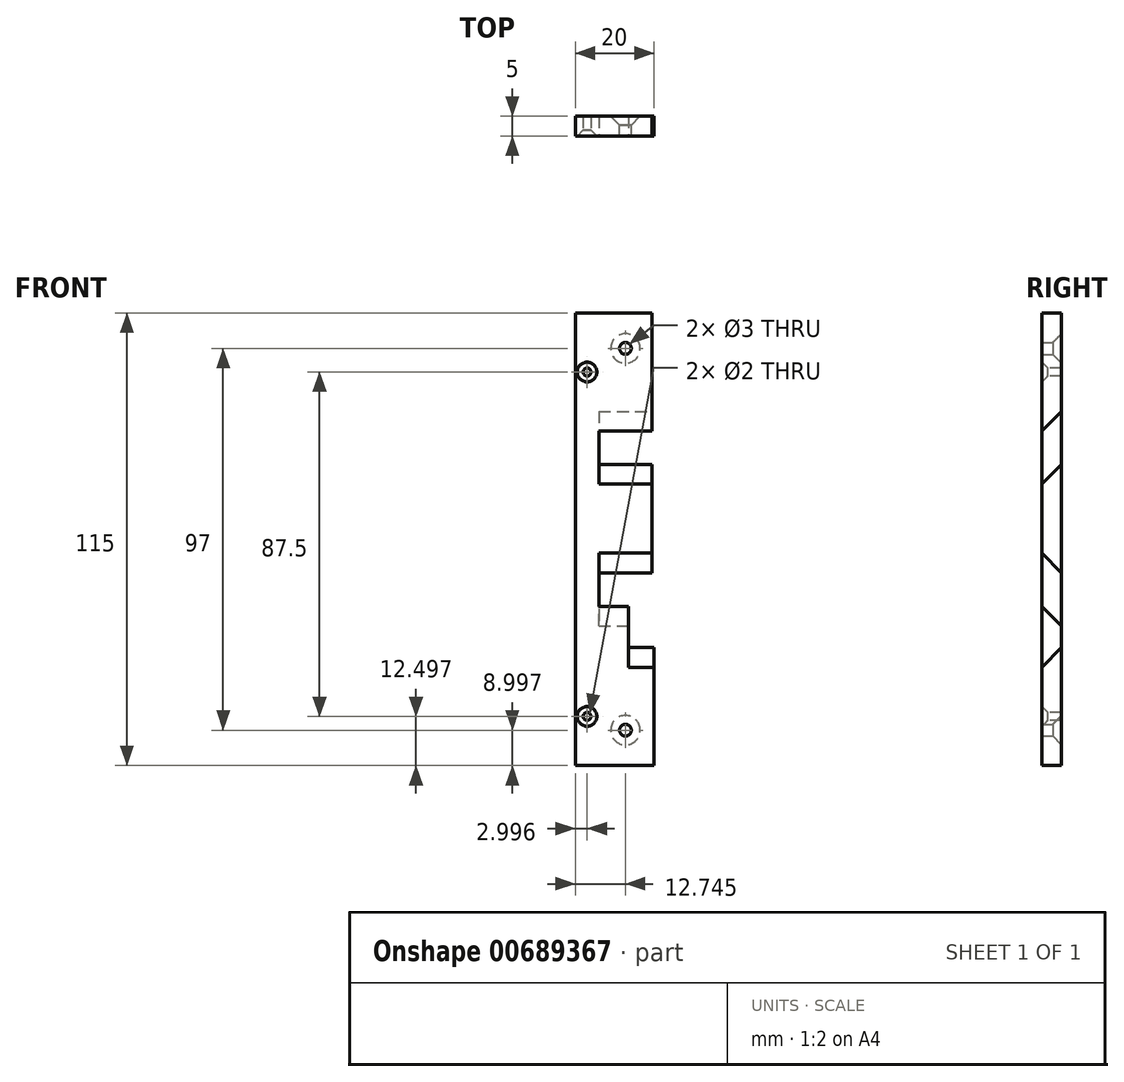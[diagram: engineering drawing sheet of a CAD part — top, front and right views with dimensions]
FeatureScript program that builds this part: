
annotation { "Feature Type Name" : "Feature", "Feature Type Description" : "" }
export const myFeature = defineFeature(function(context is Context, id is Id, definition is map)
    precondition{}
    {
        {
            var Q0;
            Q0=qCreatedBy(makeId("Front.planeOp"),FACE);
            var sketch = newSketch(context, id + "F0", { "sketchPlane" : qUnion([Q0])});
            skLineSegment(sketch, "E0.top", {"start": v(-0.37, 114.33) * mm, "end": v(19.13, 114.33) * mm});
            skLineSegment(sketch, "E0.left", {"start": v(-0.37, -0.67) * mm, "end": v(-0.37, 114.33) * mm});
            skLineSegment(sketch, "E1", {"start": v(5.63, 84.33) * mm, "end": v(5.63, 75.83) * mm});
            skLineSegment(sketch, "E2", {"start": v(5.63, 84.33) * mm, "end": v(19.13, 84.33) * mm});
            skLineSegment(sketch, "E3.trimOffspring", {"start": v(5.63, 48.33) * mm, "end": v(5.63, 39.83) * mm});
            skLineSegment(sketch, "E4", {"start": v(19.13, 114.33) * mm, "end": v(19.13, 84.33) * mm});
            skLineSegment(sketch, "E5.trimOffspring", {"start": v(19.13, 75.83) * mm, "end": v(5.63, 75.83) * mm});
            skLineSegment(sketch, "E6.trimOffspring", {"start": v(19.13, 48.33) * mm, "end": v(5.63, 48.33) * mm});
            skLineSegment(sketch, "E7.trimOffspring", {"start": v(19.63, 29.33) * mm, "end": v(13.13, 29.33) * mm});
            skLineSegment(sketch, "E8", {"start": v(19.63, 29.33) * mm, "end": v(19.63, -0.67) * mm});
            skLineSegment(sketch, "E9", {"start": v(13.13, 29.33) * mm, "end": v(13.13, 39.83) * mm});
            skLineSegment(sketch, "E10.trimOffspring", {"start": v(13.13, 39.83) * mm, "end": v(5.63, 39.83) * mm});
            skLineSegment(sketch, "E11.trimOffspring", {"start": v(19.13, 75.83) * mm, "end": v(19.13, 48.33) * mm});
            skLineSegment(sketch, "E12", {"start": v(-0.37, -0.67) * mm, "end": v(19.63, -0.67) * mm});
            skSolve(sketch);
        }
        {
            var Q0;
            Q0=qSketchRegion(id+"F0",true);
            extrude(context, id + "F1", {"entities" : qUnion([Q0]), "depth" : 5 * mm});
        }
        {
            var Q0;
            Q0=makeQuery(id+"F1.opExtrude","SWEPT_FACE",FACE,{"disambiguationData":[OSD([sQuery(id+"F0.wireOp",EDGE,"E4")])]});
            var sketch = newSketch(context, id + "F2", { "sketchPlane" : qUnion([Q0])});
            skLineSegment(sketch, "E13", {"start": v(-5, 84.33) * mm, "end": v(0, 84.33) * mm});
            skLineSegment(sketch, "E14", {"start": v(0, 84.33) * mm, "end": v(0, 89.33) * mm});
            skLineSegment(sketch, "E15", {"start": v(0, 89.33) * mm, "end": v(-5, 84.33) * mm});
            skSolve(sketch);
        }
        {
            var Q0;
            Q0=makeQuery(id+"F1.opExtrude","SWEPT_FACE",FACE,{"disambiguationData":[OSD([sQuery(id+"F0.wireOp",EDGE,"E11.trimOffspring")])]});
            var sketch = newSketch(context, id + "F3", { "sketchPlane" : qUnion([Q0])});
            skLineSegment(sketch, "E16", {"start": v(0, 75.83) * mm, "end": v(-5, 75.83) * mm});
            skLineSegment(sketch, "E17", {"start": v(-5, 75.83) * mm, "end": v(-5, 70.83) * mm});
            skLineSegment(sketch, "E18", {"start": v(-5, 70.83) * mm, "end": v(0, 75.83) * mm});
            skLineSegment(sketch, "E19", {"start": v(0, 48.33) * mm, "end": v(-5, 48.33) * mm});
            skLineSegment(sketch, "E20", {"start": v(-5, 48.33) * mm, "end": v(-5, 53.33) * mm});
            skLineSegment(sketch, "E21", {"start": v(-5, 53.33) * mm, "end": v(0, 48.33) * mm});
            skSolve(sketch);
        }
        {
            var Q0;
            Q0=qSketchRegion(id+"F2",true);
            var Q1;
            Q1=qSketchRegion(id+"F3",true);
            extrude(context, id + "F4", {"entities" : qUnion([Q0, Q1]), "operationType" : NewBodyOperationType.REMOVE, "oppositeDirection" : true, "depth" : 13.5 * mm});
        }
        {
            var Q0;
            Q0=makeQuery(id+"F1.opExtrude","SWEPT_FACE",FACE,{"disambiguationData":[OSD([sQuery(id+"F0.wireOp",EDGE,"E9")])]});
            var sketch = newSketch(context, id + "F5", { "sketchPlane" : qUnion([Q0])});
            skLineSegment(sketch, "E22", {"start": v(-5, 39.83) * mm, "end": v(0, 39.83) * mm});
            skLineSegment(sketch, "E23", {"start": v(0, 39.83) * mm, "end": v(0, 34.83) * mm});
            skLineSegment(sketch, "E24", {"start": v(0, 34.83) * mm, "end": v(-5, 39.83) * mm});
            skSolve(sketch);
        }
        {
            var Q0;
            Q0=qSketchRegion(id+"F5",true);
            extrude(context, id + "F6", {"entities" : qUnion([Q0]), "operationType" : NewBodyOperationType.REMOVE, "oppositeDirection" : true, "depth" : 7.5 * mm});
        }
        {
            var Q0;
            Q0=makeQuery(id+"F1.opExtrude","SWEPT_FACE",FACE,{"disambiguationData":[OSD([sQuery(id+"F0.wireOp",EDGE,"E8")])]});
            var sketch = newSketch(context, id + "F7", { "sketchPlane" : qUnion([Q0])});
            skLineSegment(sketch, "E25", {"start": v(0, 29.33) * mm, "end": v(-5, 29.33) * mm});
            skLineSegment(sketch, "E26", {"start": v(-5, 29.33) * mm, "end": v(-5, 24.33) * mm});
            skLineSegment(sketch, "E27", {"start": v(-5, 24.33) * mm, "end": v(0, 29.33) * mm});
            skSolve(sketch);
        }
        {
            var Q0;
            Q0=qSketchRegion(id+"F7",true);
            extrude(context, id + "F8", {"entities" : qUnion([Q0]), "operationType" : NewBodyOperationType.REMOVE, "oppositeDirection" : true, "depth" : 6.5 * mm});
        }
        {
            var Q0;
            Q0=makeQuery(id+"F1.opExtrude","CAP_FACE",FACE,{"disambiguationData":[OSD([sQuery(id+"F0.wireOp",EDGE,"E0.top"),sQuery(id+"F0.wireOp",EDGE,"E0.left"),sQuery(id+"F0.wireOp",EDGE,"E1"),sQuery(id+"F0.wireOp",EDGE,"E2"),sQuery(id+"F0.wireOp",EDGE,"E3.trimOffspring"),sQuery(id+"F0.wireOp",EDGE,"E4"),sQuery(id+"F0.wireOp",EDGE,"E5.trimOffspring"),sQuery(id+"F0.wireOp",EDGE,"E6.trimOffspring"),sQuery(id+"F0.wireOp",EDGE,"E7.trimOffspring"),sQuery(id+"F0.wireOp",EDGE,"E8"),sQuery(id+"F0.wireOp",EDGE,"E9"),sQuery(id+"F0.wireOp",EDGE,"E10.trimOffspring"),sQuery(id+"F0.wireOp",EDGE,"E11.trimOffspring"),sQuery(id+"F0.wireOp",EDGE,"E12")])],"isStart":true});
            var sketch = newSketch(context, id + "F9", { "sketchPlane" : qUnion([Q0])});
            skPoint(sketch, "E28", {"position": v(-12.38, 105.33) * mm});
            skPoint(sketch, "E29", {"position": v(-12.38, 8.33) * mm});
            skSolve(sketch);
        }
        {
            var Q0;
            Q0=sQuery(id+"F9.wireOp",VERTEX,"E28");
            var Q1;
            Q1=sQuery(id+"F9.wireOp",VERTEX,"E29");
            var Q2;
            Q2=makeQuery(id+"F1.opExtrude","SWEPT_BODY",BODY,{"disambiguationData":[OSD([sQuery(id+"F0.wireOp",EDGE,"E0.top"),sQuery(id+"F0.wireOp",EDGE,"E0.left"),sQuery(id+"F0.wireOp",EDGE,"E1"),sQuery(id+"F0.wireOp",EDGE,"E2"),sQuery(id+"F0.wireOp",EDGE,"E3.trimOffspring"),sQuery(id+"F0.wireOp",EDGE,"E4"),sQuery(id+"F0.wireOp",EDGE,"E5.trimOffspring"),sQuery(id+"F0.wireOp",EDGE,"E6.trimOffspring"),sQuery(id+"F0.wireOp",EDGE,"E7.trimOffspring"),sQuery(id+"F0.wireOp",EDGE,"E8"),sQuery(id+"F0.wireOp",EDGE,"E9"),sQuery(id+"F0.wireOp",EDGE,"E10.trimOffspring"),sQuery(id+"F0.wireOp",EDGE,"E11.trimOffspring"),sQuery(id+"F0.wireOp",EDGE,"E12")])]});
            hole(context, id + "F10", {"style" : HoleStyle.C_SINK, "endStyle" : HoleEndStyle.THROUGH, "holeDiameter" : 3 * mm, "cSinkDiameter" : 7.5 * mm, "cSinkAngle" : 90 * degree, "majorDiameter" : 5 * mm, "isTappedThrough" : true, "tappedDepth" : 12 * mm, "tapClearance" : 3, "startFromSketch" : true, "locations" : qUnion([Q0, Q1]), "scope" : qUnion([Q2])});
        }
        {
            var Q0;
            Q0=makeQuery(id+"F1.opExtrude","CAP_FACE",FACE,{"disambiguationData":[OSD([sQuery(id+"F0.wireOp",EDGE,"E0.top"),sQuery(id+"F0.wireOp",EDGE,"E0.left"),sQuery(id+"F0.wireOp",EDGE,"E1"),sQuery(id+"F0.wireOp",EDGE,"E2"),sQuery(id+"F0.wireOp",EDGE,"E3.trimOffspring"),sQuery(id+"F0.wireOp",EDGE,"E4"),sQuery(id+"F0.wireOp",EDGE,"E5.trimOffspring"),sQuery(id+"F0.wireOp",EDGE,"E6.trimOffspring"),sQuery(id+"F0.wireOp",EDGE,"E7.trimOffspring"),sQuery(id+"F0.wireOp",EDGE,"E8"),sQuery(id+"F0.wireOp",EDGE,"E9"),sQuery(id+"F0.wireOp",EDGE,"E10.trimOffspring"),sQuery(id+"F0.wireOp",EDGE,"E11.trimOffspring"),sQuery(id+"F0.wireOp",EDGE,"E12")])],"isStart":false});
            var sketch = newSketch(context, id + "F11", { "sketchPlane" : qUnion([Q0])});
            skPoint(sketch, "E30", {"position": v(2.63, 11.83) * mm});
            skPoint(sketch, "E31", {"position": v(2.63, 99.33) * mm});
            skSolve(sketch);
        }
        {
            var Q0;
            Q0=sQuery(id+"F11.wireOp",VERTEX,"E30");
            var Q1;
            Q1=sQuery(id+"F11.wireOp",VERTEX,"E31");
            var Q2;
            Q2=makeQuery(id+"F1.opExtrude","SWEPT_BODY",BODY,{"disambiguationData":[OSD([sQuery(id+"F0.wireOp",EDGE,"E0.top"),sQuery(id+"F0.wireOp",EDGE,"E0.left"),sQuery(id+"F0.wireOp",EDGE,"E1"),sQuery(id+"F0.wireOp",EDGE,"E2"),sQuery(id+"F0.wireOp",EDGE,"E3.trimOffspring"),sQuery(id+"F0.wireOp",EDGE,"E4"),sQuery(id+"F0.wireOp",EDGE,"E5.trimOffspring"),sQuery(id+"F0.wireOp",EDGE,"E6.trimOffspring"),sQuery(id+"F0.wireOp",EDGE,"E7.trimOffspring"),sQuery(id+"F0.wireOp",EDGE,"E8"),sQuery(id+"F0.wireOp",EDGE,"E9"),sQuery(id+"F0.wireOp",EDGE,"E10.trimOffspring"),sQuery(id+"F0.wireOp",EDGE,"E11.trimOffspring"),sQuery(id+"F0.wireOp",EDGE,"E12")])]});
            hole(context, id + "F12", {"style" : HoleStyle.C_SINK, "endStyle" : HoleEndStyle.THROUGH, "holeDiameter" : 2 * mm, "cSinkDiameter" : 5 * mm, "cSinkAngle" : 90 * degree, "majorDiameter" : 5 * mm, "isTappedThrough" : true, "tappedDepth" : 12 * mm, "tapClearance" : 3, "startFromSketch" : true, "locations" : qUnion([Q0, Q1]), "scope" : qUnion([Q2])});
        }
    });
